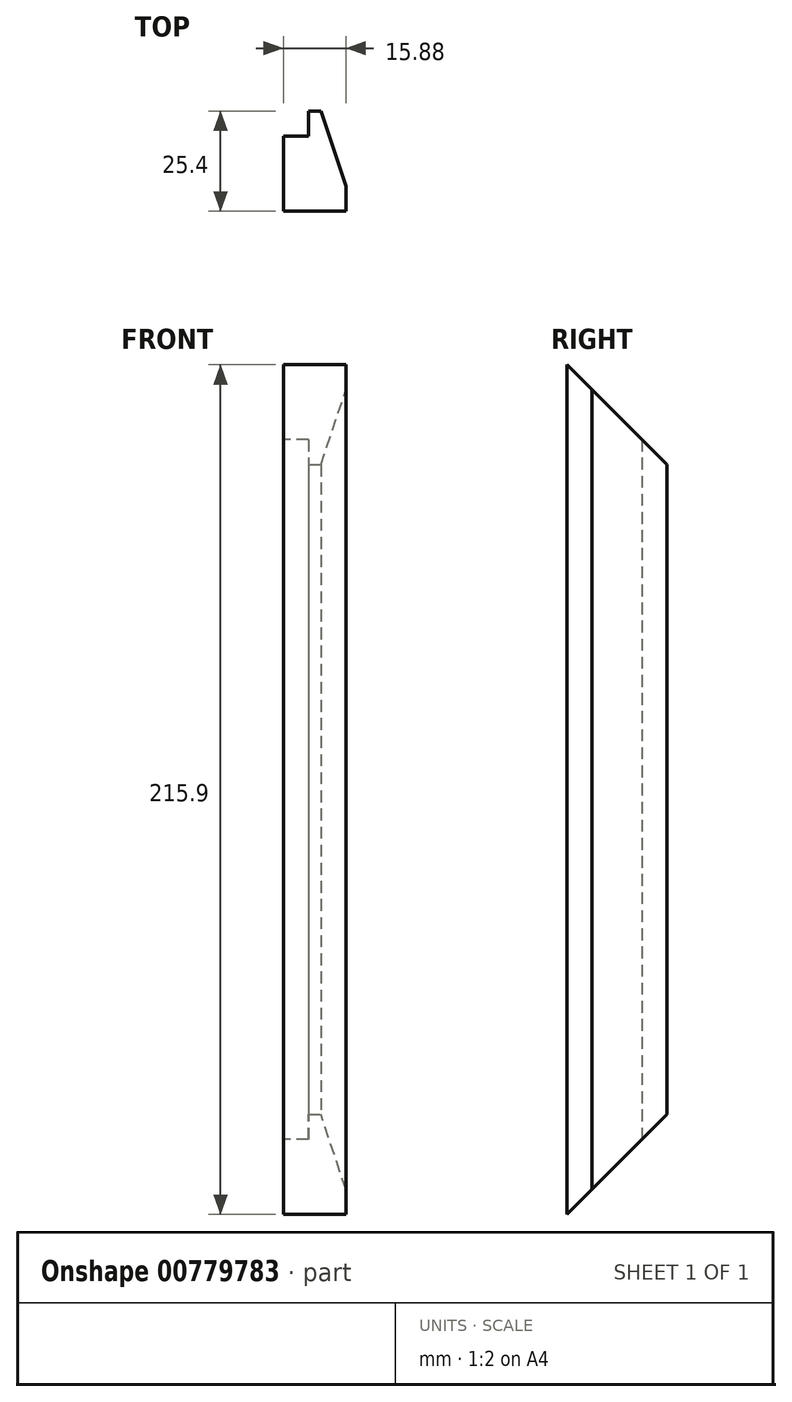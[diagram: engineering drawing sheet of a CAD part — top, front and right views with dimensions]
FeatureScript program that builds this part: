
annotation { "Feature Type Name" : "Feature", "Feature Type Description" : "" }
export const myFeature = defineFeature(function(context is Context, id is Id, definition is map)
    precondition{}
    {
        {
            var Q0;
            Q0=qCreatedBy(makeId("Right.planeOp"),FACE);
            var sketch = newSketch(context, id + "F0", { "sketchPlane" : qUnion([Q0])});
            skLineSegment(sketch, "E0.bottom", {"start": v(12.7, 107.95) * mm, "end": v(-12.7, 107.95) * mm});
            skLineSegment(sketch, "E0.top", {"start": v(12.7, -107.95) * mm, "end": v(-12.7, -107.95) * mm});
            skLineSegment(sketch, "E0.left", {"start": v(12.7, 107.95) * mm, "end": v(12.7, -107.95) * mm});
            skLineSegment(sketch, "E0.right", {"start": v(-12.7, 107.95) * mm, "end": v(-12.7, -107.95) * mm});
            skPoint(sketch, "E0.middle", {"position": v(0, 0) * mm});
            skSolve(sketch);
        }
        {
            var Q0;
            Q0 = qSketchRegion(id + "F0", true);
            extrude(context, id + "F1", {"entities" : qUnion([Q0]), "depth" : 15.88 * mm, "offsetDistance" : 25.4 * mm});
        }
        {
            var Q0;
            Q0=makeQuery(id+"F1.opExtrude","CAP_FACE",FACE,{"disambiguationData":[OSD([sQuery(id+"F0.wireOp",EDGE,"E0.bottom"),sQuery(id+"F0.wireOp",EDGE,"E0.top"),sQuery(id+"F0.wireOp",EDGE,"E0.left"),sQuery(id+"F0.wireOp",EDGE,"E0.right")])],"isStart":false});
            var sketch = newSketch(context, id + "F2", { "sketchPlane" : qUnion([Q0])});
            skLineSegment(sketch, "E1", {"start": v(-12.7, 107.95) * mm, "end": v(12.7, 82.55) * mm});
            skLineSegment(sketch, "E2", {"start": v(-12.7, -107.95) * mm, "end": v(12.7, -82.55) * mm});
            skSolve(sketch);
        }
        {
            var Q0;
            Q0=makeQuery(id+"F1.opExtrude","SWEPT_FACE",FACE,{"disambiguationData":[OSD([sQuery(id+"F0.wireOp",EDGE,"E0.top")])]});
            var sketch = newSketch(context, id + "F3", { "sketchPlane" : qUnion([Q0])});
            skLineSegment(sketch, "E3.bottom", {"start": v(0, -12.7) * mm, "end": v(6.35, -12.7) * mm});
            skLineSegment(sketch, "E3.top", {"start": v(0, -6.35) * mm, "end": v(6.35, -6.35) * mm});
            skLineSegment(sketch, "E3.left", {"start": v(0, -12.7) * mm, "end": v(0, -6.35) * mm});
            skLineSegment(sketch, "E3.right", {"start": v(6.35, -12.7) * mm, "end": v(6.35, -6.35) * mm});
            skSolve(sketch);
        }
        {
            var Q0;
            Q0=makeQuery(id+"F3.imprint","IMPRINT",FACE,{"disambiguationData":[TD([[makeQuery(id+"F3.imprint","IMPRINT",EDGE,{"derivedFrom":sQuery(id+"F3.wireOp",EDGE,"E3.bottom")}),-1.0]])]});
            extrude(context, id + "F4", {"entities" : qUnion([Q0]), "operationType" : NewBodyOperationType.REMOVE, "endBound" : BoundingType.THROUGH_ALL, "oppositeDirection" : true, "depth" : 25.4 * mm, "offsetDistance" : 25.4 * mm});
        }
        {
            var Q0;
            {var subQ0=sQuery(id+"F2.wireOp",EDGE,"E1");Q0=makeQuery(id+"F2.imprint","IMPRINT",FACE,{"disambiguationData":[TD([[makeQuery(id+"F2.imprint","IMPRINT",EDGE,{"derivedFrom":subQ0}),1.0]])]});}
            var Q1;
            {var subQ0=sQuery(id+"F2.wireOp",EDGE,"E2");Q1=makeQuery(id+"F2.imprint","IMPRINT",FACE,{"disambiguationData":[TD([[makeQuery(id+"F2.imprint","IMPRINT",EDGE,{"derivedFrom":subQ0}),-1.0]])]});}
            extrude(context, id + "F5", {"entities" : qUnion([Q0, Q1]), "operationType" : NewBodyOperationType.REMOVE, "endBound" : BoundingType.THROUGH_ALL, "oppositeDirection" : true, "depth" : 25.4 * mm, "offsetDistance" : 25.4 * mm});
        }
        {
            var Q0;
            Q0=makeQuery(id+"F1.opExtrude","CAP_EDGE",EDGE,{"disambiguationData":[OSD([sQuery(id+"F0.wireOp",EDGE,"E0.left")])],"isStart":false});
            chamfer(context, id + "F6", {"entities" : qUnion([Q0]), "chamferType" : ChamferType.OFFSET_ANGLE, "width" : 6.35 * mm, "oppositeDirection" : false, "angle" : 71.57 * degree, "tangentPropagation" : true});
        }
    });
